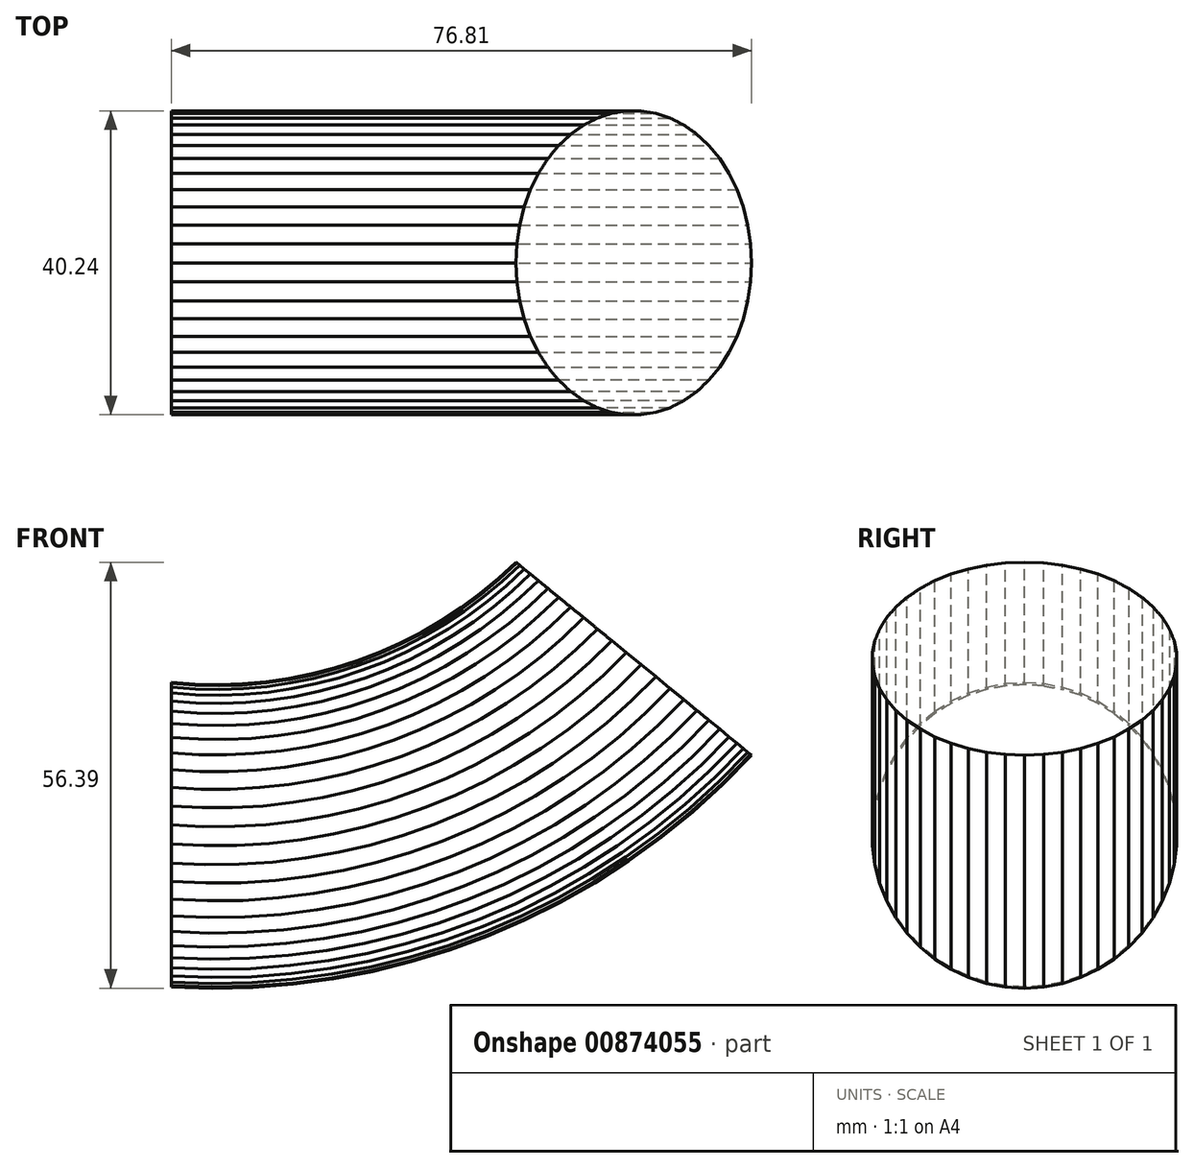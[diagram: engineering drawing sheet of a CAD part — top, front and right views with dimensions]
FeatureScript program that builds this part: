
annotation { "Feature Type Name" : "Feature", "Feature Type Description" : "" }
export const myFeature = defineFeature(function(context is Context, id is Id, definition is map)
    precondition{}
    {
        {
            var Q0;
            Q0=qCreatedBy(makeId("Right.planeOp"),FACE);
            var sketch = newSketch(context, id + "F0", { "sketchPlane" : qUnion([Q0])});
            skCircle(sketch, "E0.cCircle", {"center": v(0, 0) * mm, "radius": 20.12 * mm, "construction": true});
            skLineSegment(sketch, "E0.0", {"start": v(0, 20.16) * mm, "end": v(2.53, 20) * mm});
            skLineSegment(sketch, "E0.1", {"start": v(2.53, 20) * mm, "end": v(5.01, 19.52) * mm});
            skLineSegment(sketch, "E0.2", {"start": v(5.01, 19.52) * mm, "end": v(7.42, 18.74) * mm});
            skLineSegment(sketch, "E0.3", {"start": v(7.42, 18.74) * mm, "end": v(9.71, 17.66) * mm});
            skLineSegment(sketch, "E0.4", {"start": v(9.71, 17.66) * mm, "end": v(11.85, 16.3) * mm});
            skLineSegment(sketch, "E0.5", {"start": v(11.85, 16.3) * mm, "end": v(13.8, 14.7) * mm});
            skLineSegment(sketch, "E0.6", {"start": v(13.8, 14.7) * mm, "end": v(15.53, 12.85) * mm});
            skLineSegment(sketch, "E0.7", {"start": v(15.53, 12.85) * mm, "end": v(17.02, 10.8) * mm});
            skLineSegment(sketch, "E0.8", {"start": v(17.02, 10.8) * mm, "end": v(18.24, 8.58) * mm});
            skLineSegment(sketch, "E0.9", {"start": v(18.24, 8.58) * mm, "end": v(19.17, 6.23) * mm});
            skLineSegment(sketch, "E0.10", {"start": v(19.17, 6.23) * mm, "end": v(19.8, 3.78) * mm});
            skLineSegment(sketch, "E0.11", {"start": v(19.8, 3.78) * mm, "end": v(20.12, 1.26) * mm});
            skLineSegment(sketch, "E0.12", {"start": v(20.12, 1.26) * mm, "end": v(20.12, -1.27) * mm});
            skLineSegment(sketch, "E0.13", {"start": v(20.12, -1.27) * mm, "end": v(19.8, -3.78) * mm});
            skLineSegment(sketch, "E0.14", {"start": v(19.8, -3.78) * mm, "end": v(19.17, -6.23) * mm});
            skLineSegment(sketch, "E0.15", {"start": v(19.17, -6.23) * mm, "end": v(18.24, -8.58) * mm});
            skLineSegment(sketch, "E0.16", {"start": v(18.24, -8.58) * mm, "end": v(17.02, -10.8) * mm});
            skLineSegment(sketch, "E0.17", {"start": v(17.02, -10.8) * mm, "end": v(15.53, -12.85) * mm});
            skLineSegment(sketch, "E0.18", {"start": v(15.53, -12.85) * mm, "end": v(13.8, -14.7) * mm});
            skLineSegment(sketch, "E0.19", {"start": v(13.8, -14.7) * mm, "end": v(11.85, -16.3) * mm});
            skLineSegment(sketch, "E0.20", {"start": v(11.85, -16.3) * mm, "end": v(9.7, -17.67) * mm});
            skLineSegment(sketch, "E0.21", {"start": v(9.7, -17.67) * mm, "end": v(7.42, -18.74) * mm});
            skLineSegment(sketch, "E0.22", {"start": v(7.42, -18.74) * mm, "end": v(5.01, -19.53) * mm});
            skLineSegment(sketch, "E0.23", {"start": v(5.01, -19.53) * mm, "end": v(2.52, -20) * mm});
            skLineSegment(sketch, "E0.24", {"start": v(2.52, -20) * mm, "end": v(0, -20.16) * mm});
            skLineSegment(sketch, "E0.25", {"start": v(0, -20.16) * mm, "end": v(-2.53, -20) * mm});
            skLineSegment(sketch, "E0.26", {"start": v(-2.53, -20) * mm, "end": v(-5.01, -19.52) * mm});
            skLineSegment(sketch, "E0.27", {"start": v(-5.01, -19.52) * mm, "end": v(-7.42, -18.74) * mm});
            skLineSegment(sketch, "E0.28", {"start": v(-7.42, -18.74) * mm, "end": v(-9.71, -17.66) * mm});
            skLineSegment(sketch, "E0.29", {"start": v(-9.71, -17.66) * mm, "end": v(-11.85, -16.3) * mm});
            skLineSegment(sketch, "E0.30", {"start": v(-11.85, -16.3) * mm, "end": v(-13.8, -14.7) * mm});
            skLineSegment(sketch, "E0.31", {"start": v(-13.8, -14.7) * mm, "end": v(-15.53, -12.85) * mm});
            skLineSegment(sketch, "E0.32", {"start": v(-15.53, -12.85) * mm, "end": v(-17.02, -10.8) * mm});
            skLineSegment(sketch, "E0.33", {"start": v(-17.02, -10.8) * mm, "end": v(-18.24, -8.58) * mm});
            skLineSegment(sketch, "E0.34", {"start": v(-18.24, -8.58) * mm, "end": v(-19.17, -6.23) * mm});
            skLineSegment(sketch, "E0.35", {"start": v(-19.17, -6.23) * mm, "end": v(-19.8, -3.78) * mm});
            skLineSegment(sketch, "E0.36", {"start": v(-19.8, -3.78) * mm, "end": v(-20.12, -1.26) * mm});
            skLineSegment(sketch, "E0.37", {"start": v(-20.12, -1.26) * mm, "end": v(-20.12, 1.27) * mm});
            skLineSegment(sketch, "E0.38", {"start": v(-20.12, 1.27) * mm, "end": v(-19.8, 3.78) * mm});
            skLineSegment(sketch, "E0.39", {"start": v(-19.8, 3.78) * mm, "end": v(-19.17, 6.23) * mm});
            skLineSegment(sketch, "E0.40", {"start": v(-19.17, 6.23) * mm, "end": v(-18.24, 8.58) * mm});
            skLineSegment(sketch, "E0.41", {"start": v(-18.24, 8.58) * mm, "end": v(-17.02, 10.8) * mm});
            skLineSegment(sketch, "E0.42", {"start": v(-17.02, 10.8) * mm, "end": v(-15.53, 12.85) * mm});
            skLineSegment(sketch, "E0.43", {"start": v(-15.53, 12.85) * mm, "end": v(-13.8, 14.7) * mm});
            skLineSegment(sketch, "E0.44", {"start": v(-13.8, 14.7) * mm, "end": v(-11.85, 16.3) * mm});
            skLineSegment(sketch, "E0.45", {"start": v(-11.85, 16.3) * mm, "end": v(-9.7, 17.67) * mm});
            skLineSegment(sketch, "E0.46", {"start": v(-9.7, 17.67) * mm, "end": v(-7.42, 18.74) * mm});
            skLineSegment(sketch, "E0.47", {"start": v(-7.42, 18.74) * mm, "end": v(-5.01, 19.53) * mm});
            skLineSegment(sketch, "E0.48", {"start": v(-5.01, 19.53) * mm, "end": v(-2.52, 20) * mm});
            skLineSegment(sketch, "E0.49", {"start": v(-2.52, 20) * mm, "end": v(0, 20.16) * mm});
            skPoint(sketch, "E0.0.midPoint", {"position": v(1.27, 20.08) * mm});
            skLineSegment(sketch, "E1", {"start": v(1.3, 0) * mm, "end": v(0, 0) * mm});
            skSolve(sketch);
        }
        {
            var Q0;
            Q0=qCreatedBy(makeId("Front.planeOp"),FACE);
            var sketch = newSketch(context, id + "F1", { "sketchPlane" : qUnion([Q0])});
            skArc(sketch, "E2", {"start": v(0, 0) * mm, "mid": v(33.22, 4.75) * mm, "end": v(61.21, 23.27) * mm});
            skSolve(sketch);
        }
        {
            var Q0;
            Q0=makeQuery(id+"F0.imprint","IMPRINT",FACE,{"disambiguationData":[TD([[makeQuery(id+"F0.imprint","IMPRINT",EDGE,{"derivedFrom":sQuery(id+"F0.wireOp",EDGE,"E0.0")}),-1.0]])]});
            var Q1;
            Q1=sQuery(id+"F1.wireOp",EDGE,"E2");
            sweep(context, id + "F2", {"profiles" : qUnion([Q0]), "path" : qUnion([Q1])});
        }
    });
